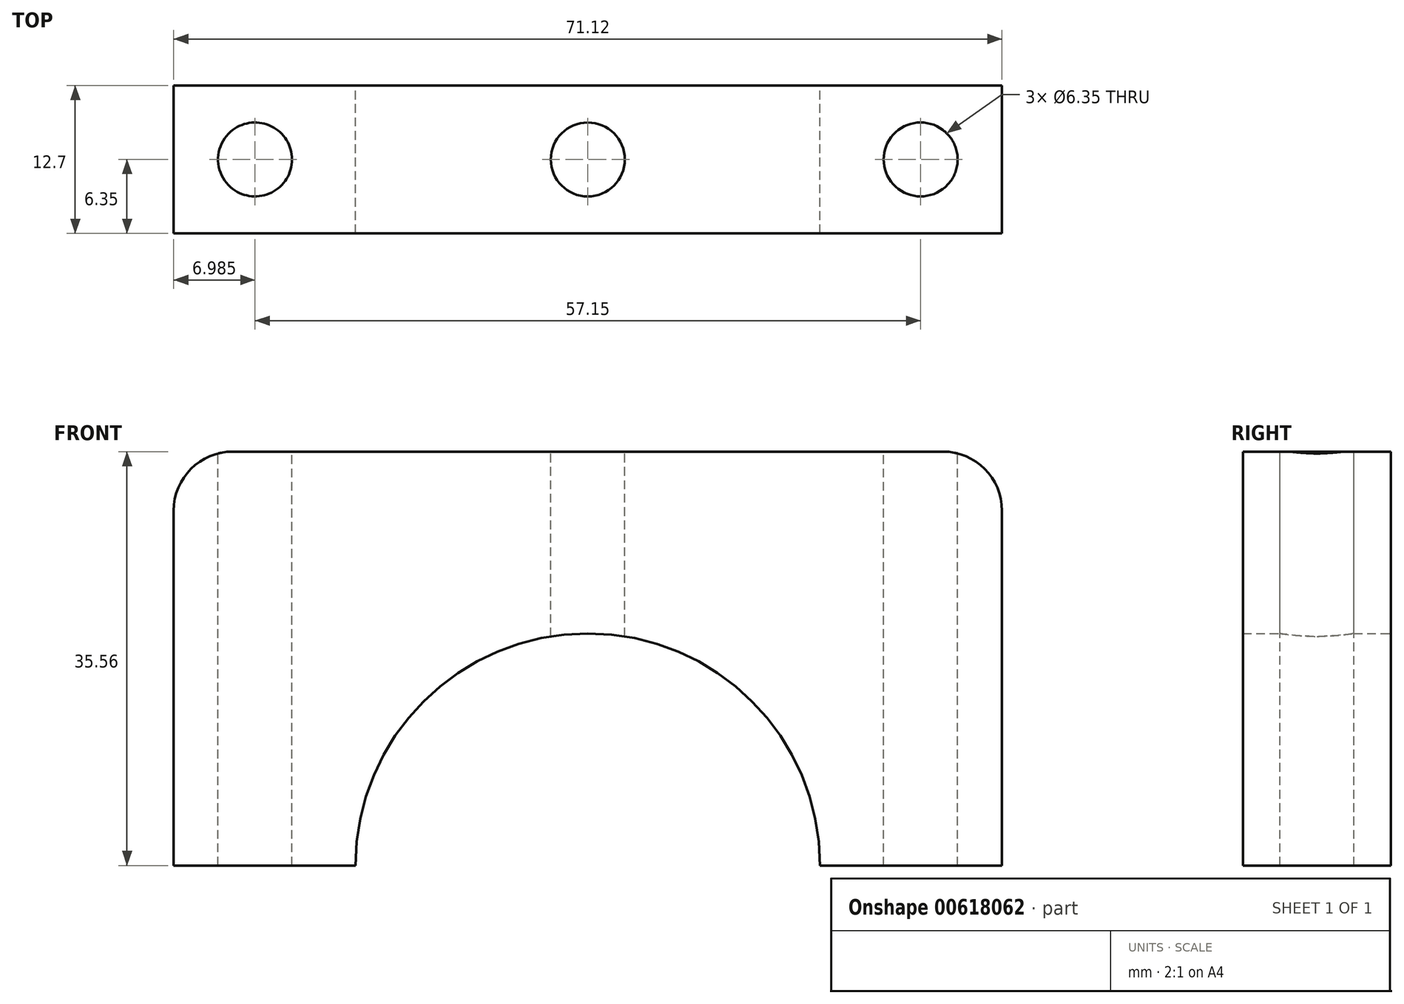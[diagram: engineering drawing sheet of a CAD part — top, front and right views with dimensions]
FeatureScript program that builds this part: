
annotation { "Feature Type Name" : "Feature", "Feature Type Description" : "" }
export const myFeature = defineFeature(function(context is Context, id is Id, definition is map)
    precondition{}
    {
        {
            var Q0;
            Q0=qCreatedBy(makeId("Front.planeOp"),FACE);
            var sketch = newSketch(context, id + "F0", { "sketchPlane" : qUnion([Q0])});
            skLineSegment(sketch, "E0.bottom", {"start": v(0, 0) * mm, "end": v(15.62, 0) * mm});
            skLineSegment(sketch, "E0.top", {"start": v(0, 35.56) * mm, "end": v(71.12, 35.56) * mm});
            skLineSegment(sketch, "E0.left", {"start": v(0, 0) * mm, "end": v(0, 35.56) * mm});
            skLineSegment(sketch, "E0.right", {"start": v(71.12, 0) * mm, "end": v(71.12, 35.56) * mm});
            skArc(sketch, "E1", {"start": v(55.5, 0) * mm, "mid": v(35.56, 19.94) * mm, "end": v(15.62, 0) * mm});
            skLineSegment(sketch, "E2.trimOffspring", {"start": v(55.5, 0) * mm, "end": v(71.12, 0) * mm});
            skSolve(sketch);
        }
        {
            var Q0;
            Q0=makeQuery(id+"F0.imprint","IMPRINT",FACE,{"disambiguationData":[TD([[makeQuery(id+"F0.imprint","IMPRINT",EDGE,{"derivedFrom":sQuery(id+"F0.wireOp",EDGE,"E0.bottom")}),1.0]])]});
            extrude(context, id + "F1", {"entities" : qUnion([Q0]), "depth" : 12.7 * mm, "offsetDistance" : 25.4 * mm});
        }
        {
            var Q0;
            Q0=makeQuery(id+"F1.opExtrude","SWEPT_FACE",FACE,{"disambiguationData":[OSD([sQuery(id+"F0.wireOp",EDGE,"E0.top")])]});
            var sketch = newSketch(context, id + "F2", { "sketchPlane" : qUnion([Q0])});
            skCircle(sketch, "E3", {"center": v(6.98, -6.35) * mm, "radius": 3.18 * mm});
            skCircle(sketch, "E4", {"center": v(64.13, -6.35) * mm, "radius": 3.18 * mm});
            skSolve(sketch);
        }
        {
            var Q0;
            Q0=makeQuery(id+"F2.imprint","IMPRINT",FACE,{"disambiguationData":[TD([[makeQuery(id+"F2.imprint","IMPRINT",EDGE,{"derivedFrom":sQuery(id+"F2.wireOp",EDGE,"E3")}),1.0]])]});
            var Q1;
            Q1=makeQuery(id+"F2.imprint","IMPRINT",FACE,{"disambiguationData":[TD([[makeQuery(id+"F2.imprint","IMPRINT",EDGE,{"derivedFrom":sQuery(id+"F2.wireOp",EDGE,"E4")}),1.0]])]});
            extrude(context, id + "F3", {"entities" : qUnion([Q0, Q1]), "operationType" : NewBodyOperationType.REMOVE, "endBound" : BoundingType.THROUGH_ALL, "oppositeDirection" : true, "depth" : 25.4 * mm, "offsetDistance" : 25.4 * mm});
        }
        {
            var Q0;
            Q0=makeQuery(id+"F1.opExtrude","SWEPT_FACE",FACE,{"disambiguationData":[OSD([sQuery(id+"F0.wireOp",EDGE,"E0.top")])]});
            var sketch = newSketch(context, id + "F4", { "sketchPlane" : qUnion([Q0])});
            skCircle(sketch, "E5", {"center": v(35.56, -6.35) * mm, "radius": 3.18 * mm});
            skSolve(sketch);
        }
        {
            var Q0;
            Q0=makeQuery(id+"F4.imprint","IMPRINT",FACE,{"disambiguationData":[TD([[makeQuery(id+"F4.imprint","IMPRINT",EDGE,{"derivedFrom":sQuery(id+"F4.wireOp",EDGE,"E5")}),1.0]])]});
            extrude(context, id + "F5", {"entities" : qUnion([Q0]), "operationType" : NewBodyOperationType.REMOVE, "endBound" : BoundingType.UP_TO_NEXT, "oppositeDirection" : true, "depth" : 7.62 * mm, "offsetDistance" : 25.4 * mm});
        }
        {
            var Q0;
            Q0=makeQuery(id+"F1.opExtrude","SWEPT_EDGE",EDGE,{"disambiguationData":[OSD([sQuery(id+"F0.wireOp",EDGE,"E0.top"),sQuery(id+"F0.wireOp",EDGE,"E0.left")])]});
            var Q1;
            Q1=makeQuery(id+"F1.opExtrude","SWEPT_EDGE",EDGE,{"disambiguationData":[OSD([sQuery(id+"F0.wireOp",EDGE,"E0.top"),sQuery(id+"F0.wireOp",EDGE,"E0.right")])]});
            fillet(context, id + "F6", {"entities" : qUnion([Q0, Q1]), "radius" : 5.08 * mm, "tangentPropagation" : true, "allowEdgeOverflow" : false});
        }
    });
